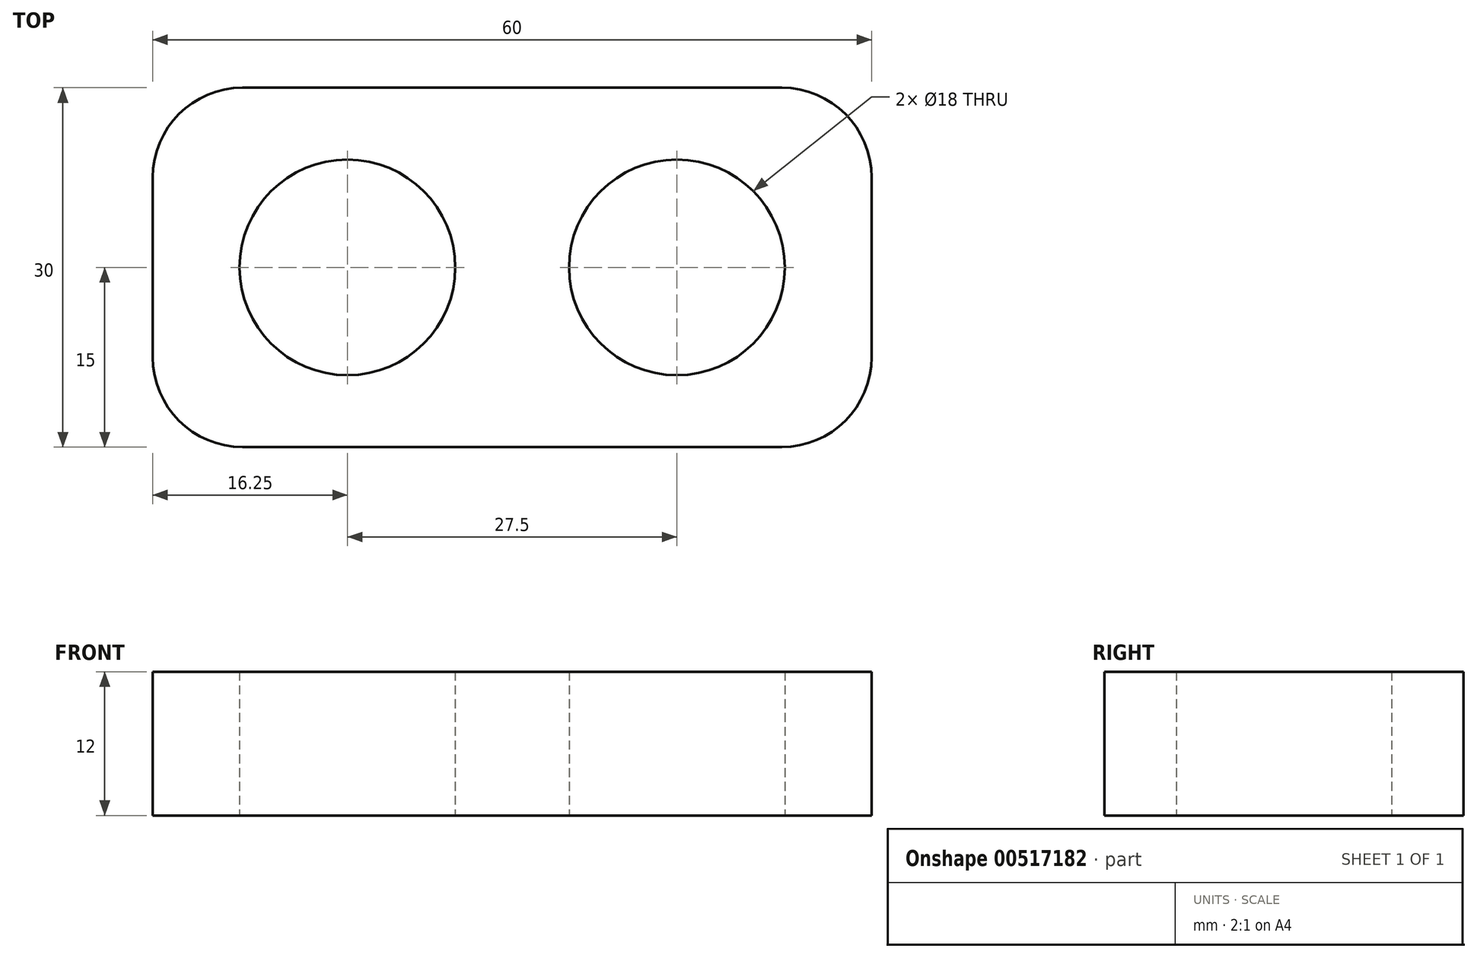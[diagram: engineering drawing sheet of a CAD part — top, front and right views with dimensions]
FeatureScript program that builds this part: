
annotation { "Feature Type Name" : "Feature", "Feature Type Description" : "" }
export const myFeature = defineFeature(function(context is Context, id is Id, definition is map)
    precondition{}
    {
        {
            var Q0;
            Q0=qCreatedBy(makeId("Top.planeOp"),FACE);
            var sketch = newSketch(context, id + "F0", { "sketchPlane" : qUnion([Q0])});
            skCircle(sketch, "E0", {"center": v(13.75, 0) * mm, "radius": 9 * mm});
            skCircle(sketch, "E1", {"center": v(-13.75, 0) * mm, "radius": 9 * mm});
            skLineSegment(sketch, "E2.bottom", {"start": v(-30, 15) * mm, "end": v(30, 15) * mm});
            skLineSegment(sketch, "E2.top", {"start": v(-30, -15) * mm, "end": v(30, -15) * mm});
            skLineSegment(sketch, "E2.left", {"start": v(-30, 15) * mm, "end": v(-30, -15) * mm});
            skLineSegment(sketch, "E2.right", {"start": v(30, 15) * mm, "end": v(30, -15) * mm});
            skSolve(sketch);
        }
        {
            var Q0;
            Q0=makeQuery(id+"F0.imprint","IMPRINT",FACE,{"disambiguationData":[TD([[makeQuery(id+"F0.imprint","IMPRINT",EDGE,{"derivedFrom":sQuery(id+"F0.wireOp",EDGE,"E0")}),-1.0]])]});
            extrude(context, id + "F1", {"entities" : qUnion([Q0]), "depth" : 12 * mm, "offsetDistance" : 25 * mm});
        }
        {
            var Q0;
            Q0=makeQuery(id+"F1.opExtrude","SWEPT_EDGE",EDGE,{"disambiguationData":[OSD([sQuery(id+"F0.wireOp",EDGE,"E2.top"),sQuery(id+"F0.wireOp",EDGE,"E2.left")])]});
            fillet(context, id + "F2", {"entities" : qUnion([Q0]), "radius" : 7.5 * mm, "tangentPropagation" : true, "allowEdgeOverflow" : false});
        }
        {
            var Q0;
            Q0=makeQuery(id+"F1.opExtrude","SWEPT_EDGE",EDGE,{"disambiguationData":[OSD([sQuery(id+"F0.wireOp",EDGE,"E2.bottom"),sQuery(id+"F0.wireOp",EDGE,"E2.left")])]});
            fillet(context, id + "F3", {"entities" : qUnion([Q0]), "radius" : 7.5 * mm, "tangentPropagation" : true, "allowEdgeOverflow" : false});
        }
        {
            var Q0;
            Q0=makeQuery(id+"F1.opExtrude","SWEPT_EDGE",EDGE,{"disambiguationData":[OSD([sQuery(id+"F0.wireOp",EDGE,"E2.top"),sQuery(id+"F0.wireOp",EDGE,"E2.right")])]});
            fillet(context, id + "F4", {"entities" : qUnion([Q0]), "radius" : 7.5 * mm, "tangentPropagation" : true, "allowEdgeOverflow" : false});
        }
        {
            var Q0;
            Q0=makeQuery(id+"F1.opExtrude","SWEPT_EDGE",EDGE,{"disambiguationData":[OSD([sQuery(id+"F0.wireOp",EDGE,"E2.bottom"),sQuery(id+"F0.wireOp",EDGE,"E2.right")])]});
            fillet(context, id + "F5", {"entities" : qUnion([Q0]), "radius" : 7.5 * mm, "tangentPropagation" : true, "allowEdgeOverflow" : false});
        }
    });
